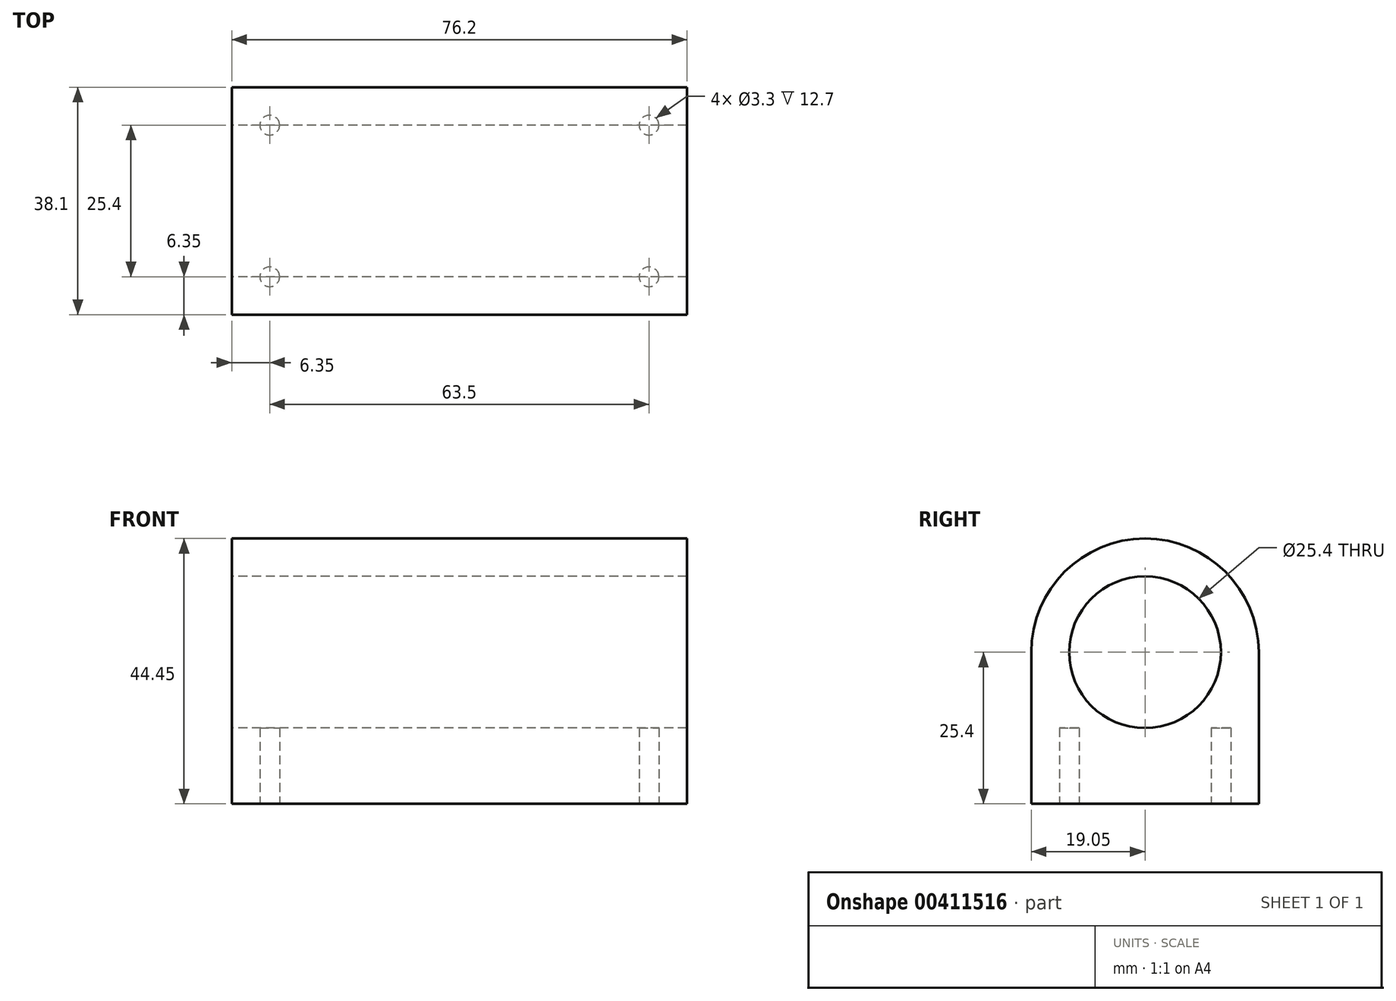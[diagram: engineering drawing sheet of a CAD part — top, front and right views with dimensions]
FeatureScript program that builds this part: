
annotation { "Feature Type Name" : "Feature", "Feature Type Description" : "" }
export const myFeature = defineFeature(function(context is Context, id is Id, definition is map)
    precondition{}
    {
        {
            var Q0;
            Q0=qCreatedBy(makeId("Right.planeOp"),FACE);
            var sketch = newSketch(context, id + "F0", { "sketchPlane" : qUnion([Q0])});
            skCircle(sketch, "E0", {"center": v(0, 0) * mm, "radius": 12.7 * mm});
            skArc(sketch, "E1", {"start": v(19.05, 0) * mm, "mid": v(0, 19.05) * mm, "end": v(-19.05, 0) * mm});
            skLineSegment(sketch, "E2", {"start": v(-19.05, 0) * mm, "end": v(-19.05, -25.4) * mm});
            skLineSegment(sketch, "E3", {"start": v(-19.05, -25.4) * mm, "end": v(19.05, -25.4) * mm});
            skLineSegment(sketch, "E4", {"start": v(19.05, -25.4) * mm, "end": v(19.05, 0) * mm});
            skSolve(sketch);
        }
        {
            var Q0;
            Q0=makeQuery(id+"F0.imprint","IMPRINT",FACE,{"disambiguationData":[TD([[makeQuery(id+"F0.imprint","IMPRINT",EDGE,{"derivedFrom":sQuery(id+"F0.wireOp",EDGE,"E0")}),-1.0]])]});
            extrude(context, id + "F1", {"entities" : qUnion([Q0]), "depth" : 76.2 * mm});
        }
        {
            var Q0;
            Q0=makeQuery(id+"F1.opExtrude","SWEPT_FACE",FACE,{"disambiguationData":[OSD([sQuery(id+"F0.wireOp",EDGE,"E3")])]});
            var sketch = newSketch(context, id + "F2", { "sketchPlane" : qUnion([Q0])});
            skCircle(sketch, "E5", {"center": v(6.35, 12.7) * mm, "radius": 1.65 * mm});
            skCircle(sketch, "E6", {"center": v(6.35, -12.7) * mm, "radius": 1.65 * mm});
            skCircle(sketch, "E7", {"center": v(69.85, -12.7) * mm, "radius": 1.65 * mm});
            skCircle(sketch, "E8", {"center": v(69.85, 12.7) * mm, "radius": 1.65 * mm});
            skSolve(sketch);
        }
        {
            var Q0;
            Q0=makeQuery(id+"F2.imprint","IMPRINT",FACE,{"disambiguationData":[TD([[makeQuery(id+"F2.imprint","IMPRINT",EDGE,{"derivedFrom":sQuery(id+"F2.wireOp",EDGE,"E5")}),1.0]])]});
            var Q1;
            Q1=makeQuery(id+"F2.imprint","IMPRINT",FACE,{"disambiguationData":[TD([[makeQuery(id+"F2.imprint","IMPRINT",EDGE,{"derivedFrom":sQuery(id+"F2.wireOp",EDGE,"E8")}),1.0]])]});
            var Q2;
            Q2=makeQuery(id+"F2.imprint","IMPRINT",FACE,{"disambiguationData":[TD([[makeQuery(id+"F2.imprint","IMPRINT",EDGE,{"derivedFrom":sQuery(id+"F2.wireOp",EDGE,"E7")}),1.0]])]});
            var Q3;
            Q3=makeQuery(id+"F2.imprint","IMPRINT",FACE,{"disambiguationData":[TD([[makeQuery(id+"F2.imprint","IMPRINT",EDGE,{"derivedFrom":sQuery(id+"F2.wireOp",EDGE,"E6")}),1.0]])]});
            extrude(context, id + "F3", {"entities" : qUnion([Q0, Q1, Q2, Q3]), "operationType" : NewBodyOperationType.REMOVE, "oppositeDirection" : true, "depth" : 12.7 * mm});
        }
    });
